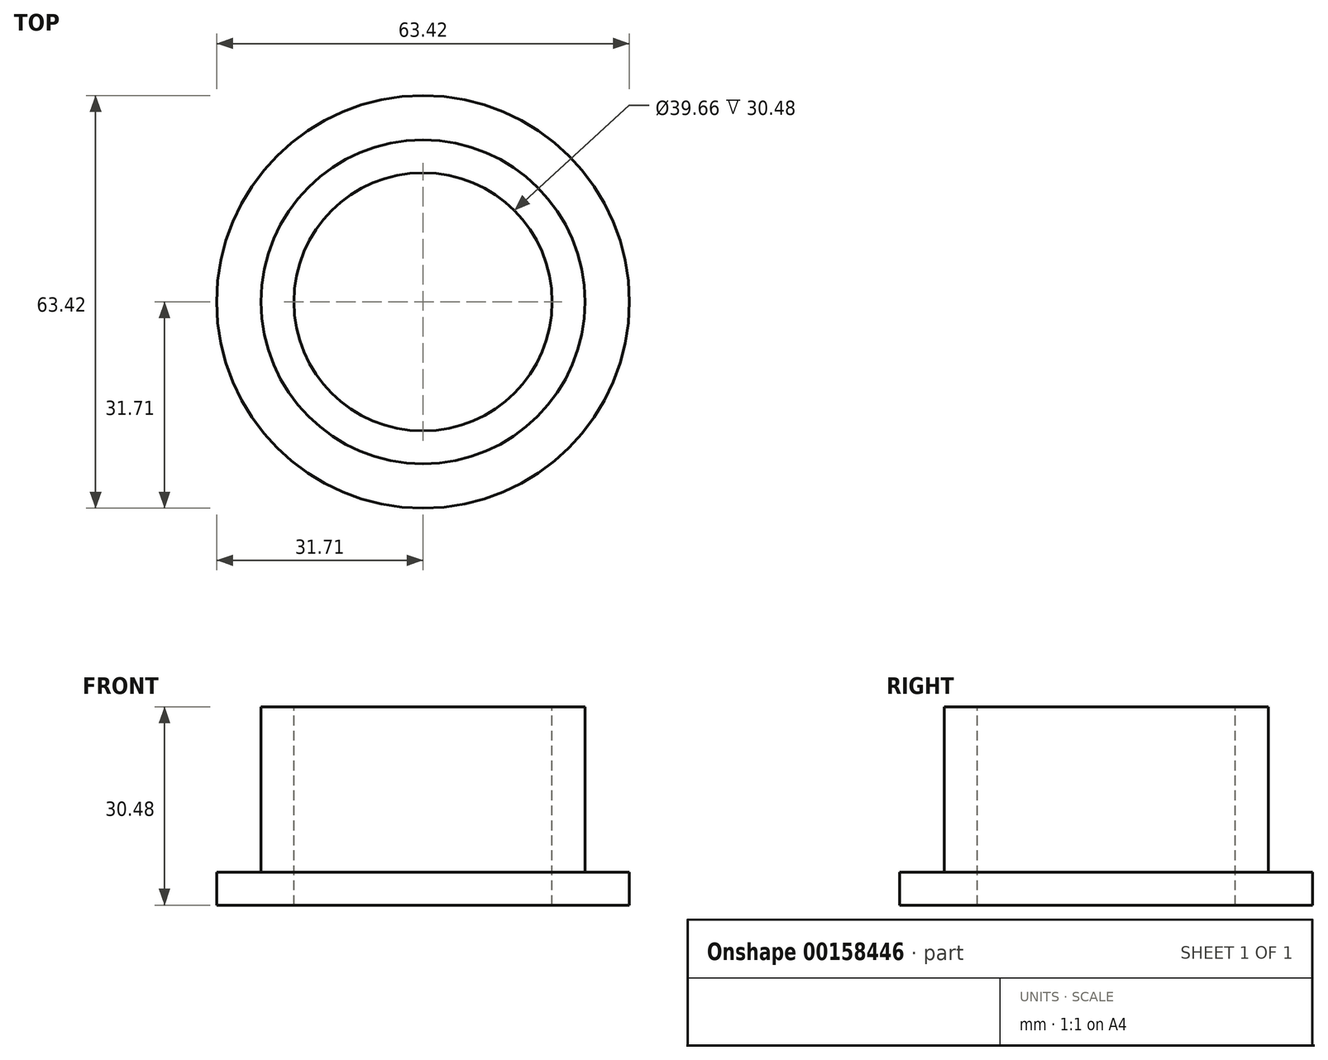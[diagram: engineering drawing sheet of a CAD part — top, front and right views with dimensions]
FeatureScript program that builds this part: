
annotation { "Feature Type Name" : "Feature", "Feature Type Description" : "" }
export const myFeature = defineFeature(function(context is Context, id is Id, definition is map)
    precondition{}
    {
        {
            var Q0;
            Q0=qCreatedBy(makeId("Top.planeOp"),FACE);
            var sketch = newSketch(context, id + "F0", { "sketchPlane" : qUnion([Q0])});
            skCircle(sketch, "E0", {"center": v(0, 0) * mm, "radius": 24.89 * mm});
            skSolve(sketch);
        }
        {
            var Q0;
            Q0=makeQuery(id+"F0.imprint","IMPRINT",FACE,{"disambiguationData":[TD([[makeQuery(id+"F0.imprint","IMPRINT",EDGE,{"derivedFrom":sQuery(id+"F0.wireOp",EDGE,"E0")}),1.0]])]});
            extrude(context, id + "F1", {"entities" : qUnion([Q0]), "depth" : 25.4 * mm});
        }
        {
            var Q0;
            Q0=qCreatedBy(makeId("Top.planeOp"),FACE);
            var sketch = newSketch(context, id + "F2", { "sketchPlane" : qUnion([Q0])});
            skCircle(sketch, "E1", {"center": v(0, 0) * mm, "radius": 31.71 * mm});
            skSolve(sketch);
        }
        {
            var Q0;
            Q0 = qSketchRegion(id + "F2", true);
            extrude(context, id + "F3", {"entities" : qUnion([Q0]), "operationType" : NewBodyOperationType.ADD, "oppositeDirection" : true, "depth" : 5.08 * mm});
        }
        {
            var Q0;
            Q0=makeQuery(id+"F1.opExtrude","CAP_FACE",FACE,{"disambiguationData":[OSD([sQuery(id+"F0.wireOp",EDGE,"E0")])],"isStart":false});
            var sketch = newSketch(context, id + "F4", { "sketchPlane" : qUnion([Q0])});
            skCircle(sketch, "E2", {"center": v(0, 0) * mm, "radius": 19.83 * mm});
            skSolve(sketch);
        }
        {
            var Q0;
            Q0 = qSketchRegion(id + "F4", true);
            extrude(context, id + "F5", {"entities" : qUnion([Q0]), "operationType" : NewBodyOperationType.REMOVE, "oppositeDirection" : true, "depth" : 38.1 * mm});
        }
    });
